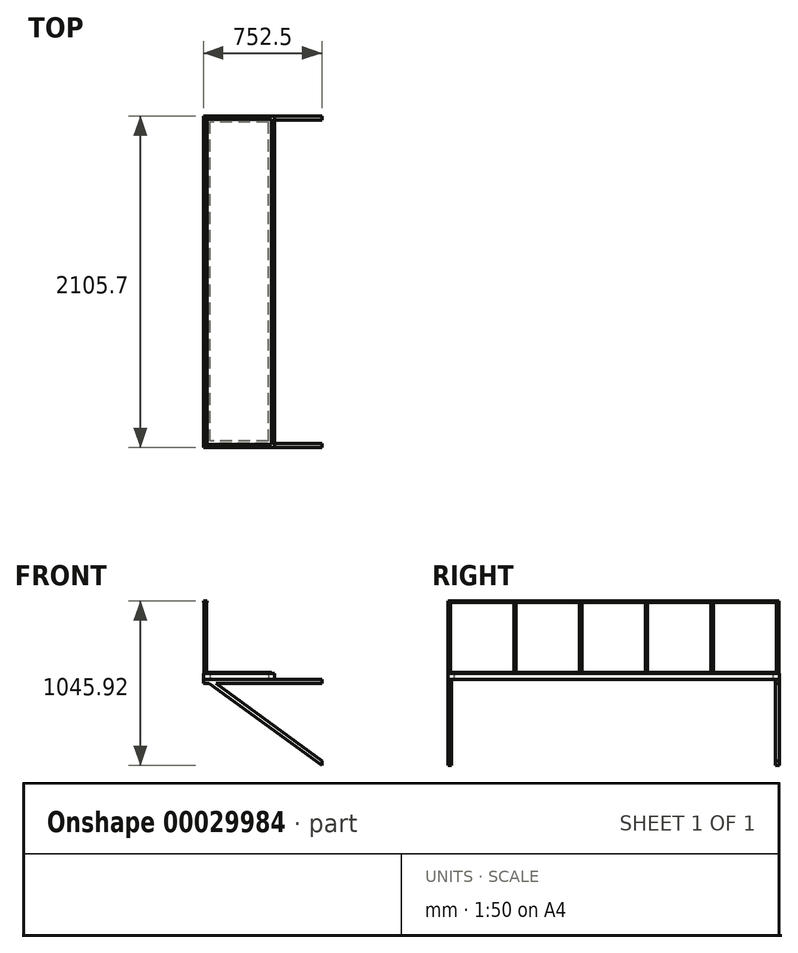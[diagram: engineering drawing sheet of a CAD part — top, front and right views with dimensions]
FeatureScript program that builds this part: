
annotation { "Feature Type Name" : "Feature", "Feature Type Description" : "" }
export const myFeature = defineFeature(function(context is Context, id is Id, definition is map)
    precondition{}
    {
        {
            var Q0;
            Q0=qCreatedBy(makeId("Top.planeOp"),FACE);
            var sketch = newSketch(context, id + "F0", { "sketchPlane" : qUnion([Q0])});
            skLineSegment(sketch, "E0.rect.bottom", {"start": v(225, -1052.85) * mm, "end": v(-225, -1052.85) * mm});
            skLineSegment(sketch, "E0.rect.top", {"start": v(225, 1052.85) * mm, "end": v(-225, 1052.85) * mm});
            skLineSegment(sketch, "E0.rect.left", {"start": v(225, -1052.85) * mm, "end": v(225, 1052.85) * mm});
            skLineSegment(sketch, "E0.rect.right", {"start": v(-225, -1052.85) * mm, "end": v(-225, 1052.85) * mm});
            skPoint(sketch, "E0.rect.middle", {"position": v(0, 0) * mm});
            skLineSegment(sketch, "E1.0", {"start": v(-185, -1012.85) * mm, "end": v(-185, 1012.85) * mm});
            skLineSegment(sketch, "E1.1", {"start": v(185, -1012.85) * mm, "end": v(-185, -1012.85) * mm});
            skLineSegment(sketch, "E1.2", {"start": v(185, -1012.85) * mm, "end": v(185, 1012.85) * mm});
            skLineSegment(sketch, "E1.3", {"start": v(185, 1012.85) * mm, "end": v(-185, 1012.85) * mm});
            skSolve(sketch);
        }
        {
            var Q0;
            Q0 = qSketchRegion(id + "F0", true);
            extrude(context, id + "F1", {"entities" : qUnion([Q0]), "depth" : 40 * mm});
        }
        {
            var Q0;
            Q0=makeQuery(id+"F1.opExtrude","CAP_FACE",FACE,{"disambiguationData":[OSD([sQuery(id+"F0.wireOp",EDGE,"E0.rect.bottom"),sQuery(id+"F0.wireOp",EDGE,"E0.rect.top"),sQuery(id+"F0.wireOp",EDGE,"E0.rect.left"),sQuery(id+"F0.wireOp",EDGE,"E0.rect.right"),sQuery(id+"F0.wireOp",EDGE,"E1.0"),sQuery(id+"F0.wireOp",EDGE,"E1.1"),sQuery(id+"F0.wireOp",EDGE,"E1.2"),sQuery(id+"F0.wireOp",EDGE,"E1.3")])],"isStart":false});
            var sketch = newSketch(context, id + "F2", { "sketchPlane" : qUnion([Q0])});
            skLineSegment(sketch, "E2.rect.bottom", {"start": v(205, -1032.85) * mm, "end": v(-205, -1032.85) * mm});
            skLineSegment(sketch, "E2.rect.top", {"start": v(205, 1032.85) * mm, "end": v(-205, 1032.85) * mm});
            skLineSegment(sketch, "E2.rect.left", {"start": v(205, -1032.85) * mm, "end": v(205, 1032.85) * mm});
            skLineSegment(sketch, "E2.rect.right", {"start": v(-205, -1032.85) * mm, "end": v(-205, 1032.85) * mm});
            skPoint(sketch, "E2.rect.middle", {"position": v(0, 0) * mm});
            skSolve(sketch);
        }
        {
            var Q0;
            Q0 = qSketchRegion(id + "F2", true);
            extrude(context, id + "F3", {"entities" : qUnion([Q0]), "operationType" : NewBodyOperationType.ADD, "depth" : 5 * mm});
        }
        {
            var Q0;
            Q0=makeQuery(id+"F1.opExtrude","CAP_FACE",FACE,{"disambiguationData":[OSD([sQuery(id+"F0.wireOp",EDGE,"E0.rect.bottom"),sQuery(id+"F0.wireOp",EDGE,"E0.rect.top"),sQuery(id+"F0.wireOp",EDGE,"E0.rect.left"),sQuery(id+"F0.wireOp",EDGE,"E0.rect.right"),sQuery(id+"F0.wireOp",EDGE,"E1.0"),sQuery(id+"F0.wireOp",EDGE,"E1.1"),sQuery(id+"F0.wireOp",EDGE,"E1.2"),sQuery(id+"F0.wireOp",EDGE,"E1.3")])],"isStart":false});
            var sketch = newSketch(context, id + "F4", { "sketchPlane" : qUnion([Q0])});
            skCircle(sketch, "E3", {"center": v(-215, -1042.85) * mm, "radius": 7.5 * mm});
            skLineSegment(sketch, "E4", {"start": v(-225, -1052.85) * mm, "end": v(-205, -1032.84) * mm, "construction": true});
            skLineSegment(sketch, "E5", {"start": v(-215, -1042.85) * mm, "end": v(-215, -625.7) * mm, "construction": true});
            skLineSegment(sketch, "E6", {"start": v(-215, -625.7) * mm, "end": v(-215, -208.57) * mm, "construction": true});
            skLineSegment(sketch, "E7", {"start": v(-215, -208.57) * mm, "end": v(-215, 208.57) * mm, "construction": true});
            skLineSegment(sketch, "E8", {"start": v(-215, 208.57) * mm, "end": v(-215, 625.7) * mm, "construction": true});
            skLineSegment(sketch, "E9", {"start": v(-215, 625.7) * mm, "end": v(-215, 1042.85) * mm, "construction": true});
            skCircle(sketch, "E10", {"center": v(-215, -625.7) * mm, "radius": 7.5 * mm});
            skCircle(sketch, "E11", {"center": v(-215, -208.57) * mm, "radius": 7.5 * mm});
            skCircle(sketch, "E12", {"center": v(-215, 208.57) * mm, "radius": 7.5 * mm});
            skCircle(sketch, "E13", {"center": v(-215, 625.7) * mm, "radius": 7.5 * mm});
            skCircle(sketch, "E14", {"center": v(-215, 1042.85) * mm, "radius": 7.5 * mm});
            skLineSegment(sketch, "E15", {"start": v(-225, 1052.85) * mm, "end": v(-205, 1032.85) * mm, "construction": true});
            skSolve(sketch);
        }
        {
            var Q0;
            Q0 = qSketchRegion(id + "F4", true);
            extrude(context, id + "F5", {"entities" : qUnion([Q0]), "operationType" : NewBodyOperationType.ADD, "depth" : 450 * mm});
        }
        {
            var Q0;
            Q0=makeQuery(id+"F5.opExtrude","CAP_FACE",FACE,{"disambiguationData":[OSD([sQuery(id+"F4.wireOp",EDGE,"E3")])],"isStart":false});
            var sketch = newSketch(context, id + "F6", { "sketchPlane" : qUnion([Q0])});
            skCircle(sketch, "E16", {"center": v(-215, 1042.85) * mm, "radius": 7.5 * mm, "construction": true});
            skLineSegment(sketch, "E17", {"start": v(-215, 1042.85) * mm, "end": v(-215, -1042.85) * mm, "construction": true});
            skCircle(sketch, "E18", {"center": v(-215, -1042.85) * mm, "radius": 7.5 * mm, "construction": true});
            skLineSegment(sketch, "E19.rect.bottom", {"start": v(-202.5, -1050.34) * mm, "end": v(-227.5, -1050.34) * mm});
            skLineSegment(sketch, "E19.rect.top", {"start": v(-202.5, 1050.34) * mm, "end": v(-227.5, 1050.34) * mm});
            skLineSegment(sketch, "E19.rect.left", {"start": v(-202.5, -1050.34) * mm, "end": v(-202.5, 1050.34) * mm});
            skLineSegment(sketch, "E19.rect.right", {"start": v(-227.5, -1050.34) * mm, "end": v(-227.5, 1050.34) * mm});
            skPoint(sketch, "E19.rect.middle", {"position": v(-215, 0) * mm});
            skSolve(sketch);
        }
        {
            var Q0;
            Q0 = qSketchRegion(id + "F6", true);
            extrude(context, id + "F7", {"entities" : qUnion([Q0]), "operationType" : NewBodyOperationType.ADD, "depth" : 10 * mm});
        }
        {
            var Q0;
            Q0=makeQuery(id+"F1.opExtrude","SWEPT_FACE",FACE,{"disambiguationData":[OSD([sQuery(id+"F0.wireOp",EDGE,"E0.rect.bottom")])]});
            var sketch = newSketch(context, id + "F8", { "sketchPlane" : qUnion([Q0])});
            skLineSegment(sketch, "E20", {"start": v(-225, 0) * mm, "end": v(525, 0) * mm});
            skLineSegment(sketch, "E21", {"start": v(-225, 0) * mm, "end": v(-225, -25) * mm});
            skLineSegment(sketch, "E22", {"start": v(-225, -25) * mm, "end": v(525, -25) * mm});
            skLineSegment(sketch, "E23", {"start": v(525, -25) * mm, "end": v(525, 0) * mm});
            skLineSegment(sketch, "E24", {"start": v(-190.65, -25) * mm, "end": v(525, -545.92) * mm});
            skLineSegment(sketch, "E25", {"start": v(525, -545.92) * mm, "end": v(525, -515) * mm});
            skLineSegment(sketch, "E26", {"start": v(525, -515) * mm, "end": v(-148.17, -25) * mm});
            skLineSegment(sketch, "E27", {"start": v(-225, 0) * mm, "end": v(-190.65, -25) * mm, "construction": true});
            skSolve(sketch);
        }
        {
            var Q0;
            {var subQ4=sQuery(id+"F8.wireOp",EDGE,"E21");Q0=makeQuery(id+"F8.imprint","IMPRINT",FACE,{"disambiguationData":[TD([[makeQuery(id+"F8.imprint","IMPRINT",EDGE,{"derivedFrom":subQ4}),1.0]])]});}
            var Q1;
            {var subQ1=sQuery(id+"F8.wireOp",EDGE,"E24");Q1=makeQuery(id+"F8.imprint","IMPRINT",FACE,{"disambiguationData":[TD([[makeQuery(id+"F8.imprint","IMPRINT",EDGE,{"derivedFrom":subQ1}),1.0]])]});}
            extrude(context, id + "F9", {"entities" : qUnion([Q0, Q1]), "oppositeDirection" : true, "depth" : 25 * mm});
        }
        {
            var Q0;
            Q0=makeQuery(id+"F9.opExtrude","SWEPT_BODY",BODY,{"disambiguationData":[OSD([sQuery(id+"F8.wireOp",EDGE,"E20"),sQuery(id+"F8.wireOp",EDGE,"E21"),sQuery(id+"F8.wireOp",EDGE,"E22"),sQuery(id+"F8.wireOp",EDGE,"E23"),sQuery(id+"F8.wireOp",EDGE,"E24"),sQuery(id+"F8.wireOp",EDGE,"E25"),sQuery(id+"F8.wireOp",EDGE,"E26")])]});
            var Q1;
            Q1=qCreatedBy(makeId("Front.planeOp"),FACE);
            mirror(context, id + "F10", {"entities" : qUnion([Q0]), "mirrorPlane" : qUnion([Q1])});
        }
    });
